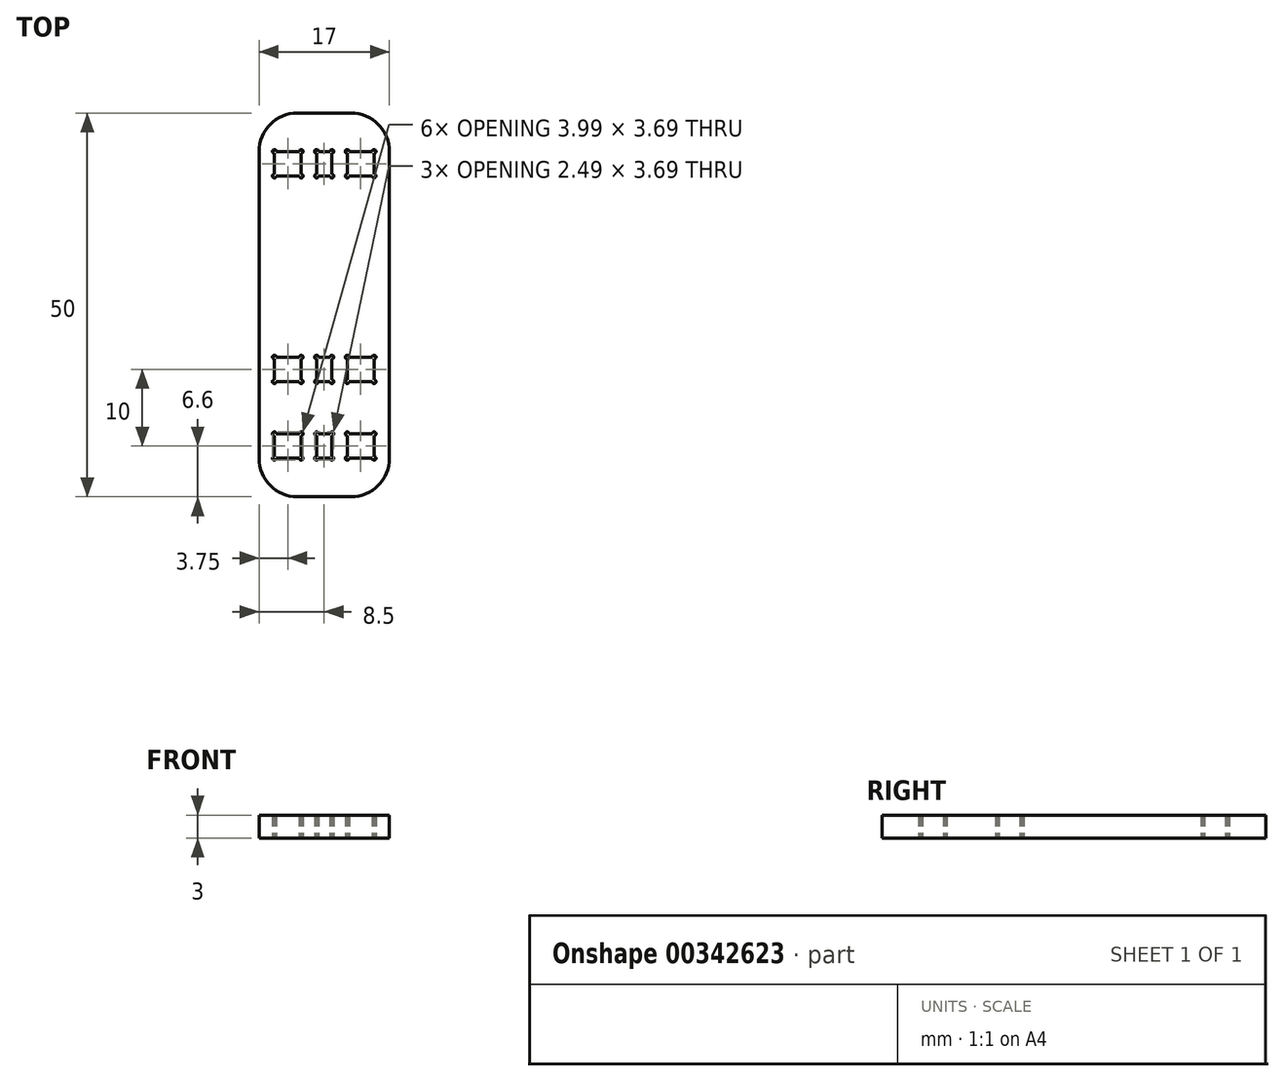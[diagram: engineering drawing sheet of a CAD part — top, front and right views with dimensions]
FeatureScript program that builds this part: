
annotation { "Feature Type Name" : "Feature", "Feature Type Description" : "" }
export const myFeature = defineFeature(function(context is Context, id is Id, definition is map)
    precondition{}
    {
        {
            var Q0;
            Q0=qCreatedBy(makeId("Top.planeOp"),FACE);
            var sketch = newSketch(context, id + "F0", { "sketchPlane" : qUnion([Q0])});
            skLineSegment(sketch, "E0.bottom", {"start": v(-3.5, 50) * mm, "end": v(3.5, 50) * mm});
            skLineSegment(sketch, "E0.top", {"start": v(-3.5, 0) * mm, "end": v(3.5, 0) * mm});
            skLineSegment(sketch, "E0.left", {"start": v(-8.5, 45) * mm, "end": v(-8.5, 5) * mm});
            skLineSegment(sketch, "E0.right", {"start": v(8.5, 45) * mm, "end": v(8.5, 5) * mm});
            skLineSegment(sketch, "E1.bottom", {"start": v(-6.5, 8.2) * mm, "end": v(-3, 8.2) * mm});
            skLineSegment(sketch, "E1.top", {"start": v(-6.5, 5) * mm, "end": v(-3, 5) * mm});
            skLineSegment(sketch, "E1.left", {"start": v(-6.5, 8.2) * mm, "end": v(-6.5, 5) * mm});
            skLineSegment(sketch, "E1.right", {"start": v(-3, 8.2) * mm, "end": v(-3, 5) * mm});
            skLineSegment(sketch, "E2.bottom", {"start": v(-1, 8.2) * mm, "end": v(1, 8.2) * mm});
            skLineSegment(sketch, "E2.top", {"start": v(-1, 5) * mm, "end": v(1, 5) * mm});
            skLineSegment(sketch, "E2.left", {"start": v(-1, 8.2) * mm, "end": v(-1, 5) * mm});
            skLineSegment(sketch, "E2.right", {"start": v(1, 8.2) * mm, "end": v(1, 5) * mm});
            skLineSegment(sketch, "E3.bottom", {"start": v(3, 8.2) * mm, "end": v(6.5, 8.2) * mm});
            skLineSegment(sketch, "E3.top", {"start": v(3, 5) * mm, "end": v(6.5, 5) * mm});
            skLineSegment(sketch, "E3.left", {"start": v(3, 8.2) * mm, "end": v(3, 5) * mm});
            skLineSegment(sketch, "E3.right", {"start": v(6.5, 8.2) * mm, "end": v(6.5, 5) * mm});
            skPoint(sketch, "E4", {"position": v(0, 5) * mm});
            skPoint(sketch, "E5", {"position": v(0, 0) * mm});
            skLineSegment(sketch, "E6", {"start": v(0, 5) * mm, "end": v(0, 0) * mm, "construction": true});
            skCircle(sketch, "E7", {"center": v(-6.5, 8.2) * mm, "radius": 0.25 * mm});
            skCircle(sketch, "E8", {"center": v(-3, 8.2) * mm, "radius": 0.25 * mm});
            skCircle(sketch, "E9", {"center": v(-3, 5) * mm, "radius": 0.25 * mm});
            skCircle(sketch, "E10", {"center": v(-6.5, 5) * mm, "radius": 0.25 * mm});
            skCircle(sketch, "E11", {"center": v(-1, 5) * mm, "radius": 0.25 * mm});
            skCircle(sketch, "E12", {"center": v(-1, 8.2) * mm, "radius": 0.25 * mm});
            skCircle(sketch, "E13.MirrorC", {"center": v(6.5, 5) * mm, "radius": 0.25 * mm});
            skCircle(sketch, "E14.MirrorC", {"center": v(6.5, 8.2) * mm, "radius": 0.25 * mm});
            skCircle(sketch, "E15.MirrorC", {"center": v(3, 8.2) * mm, "radius": 0.25 * mm});
            skCircle(sketch, "E16.MirrorC", {"center": v(3, 5) * mm, "radius": 0.25 * mm});
            skCircle(sketch, "E17.MirrorC", {"center": v(1, 5) * mm, "radius": 0.25 * mm});
            skCircle(sketch, "E18.MirrorC", {"center": v(1, 8.2) * mm, "radius": 0.25 * mm});
            skLineSegment(sketch, "E19", {"start": v(-8.5, 25) * mm, "end": v(8.5, 25) * mm, "construction": true});
            skLineSegment(sketch, "E20.MirrorCS", {"start": v(1, 5) * mm, "end": v(-1, 5) * mm});
            skLineSegment(sketch, "E21.MirrorCS", {"start": v(1, 8.2) * mm, "end": v(-1, 8.2) * mm});
            skLineSegment(sketch, "E22.MirrorCS", {"start": v(6.5, 5) * mm, "end": v(3, 5) * mm});
            skLineSegment(sketch, "E23.MirrorCS", {"start": v(6.5, 8.2) * mm, "end": v(3, 8.2) * mm});
            skLineSegment(sketch, "E24.MirrorCS", {"start": v(-3, 8.2) * mm, "end": v(-6.5, 8.2) * mm});
            skLineSegment(sketch, "E25.MirrorCS", {"start": v(-3, 5) * mm, "end": v(-6.5, 5) * mm});
            skLineSegment(sketch, "E26.MirrorCS", {"start": v(8.5, 25) * mm, "end": v(-8.5, 25) * mm, "construction": true});
            skCircle(sketch, "E27.MirrorC", {"center": v(-3, 45) * mm, "radius": 0.25 * mm});
            skCircle(sketch, "E28.MirrorC", {"center": v(-1, 45) * mm, "radius": 0.25 * mm});
            skCircle(sketch, "E29.MirrorC", {"center": v(-6.5, 41.8) * mm, "radius": 0.25 * mm});
            skCircle(sketch, "E30.MirrorC", {"center": v(-6.5, 45) * mm, "radius": 0.25 * mm});
            skLineSegment(sketch, "E31.MirrorCS", {"start": v(1, 45) * mm, "end": v(-1, 45) * mm});
            skCircle(sketch, "E32.MirrorC", {"center": v(-1, 41.8) * mm, "radius": 0.25 * mm});
            skCircle(sketch, "E33.MirrorC", {"center": v(6.5, 45) * mm, "radius": 0.25 * mm});
            skCircle(sketch, "E34.MirrorC", {"center": v(3, 41.8) * mm, "radius": 0.25 * mm});
            skCircle(sketch, "E35.MirrorC", {"center": v(3, 45) * mm, "radius": 0.25 * mm});
            skCircle(sketch, "E36.MirrorC", {"center": v(6.5, 41.8) * mm, "radius": 0.25 * mm});
            skLineSegment(sketch, "E37.MirrorCS", {"start": v(1, 41.8) * mm, "end": v(-1, 41.8) * mm});
            skCircle(sketch, "E38.MirrorC", {"center": v(1, 45) * mm, "radius": 0.25 * mm});
            skCircle(sketch, "E39.MirrorC", {"center": v(-3, 41.8) * mm, "radius": 0.25 * mm});
            skCircle(sketch, "E40.MirrorC", {"center": v(1, 41.8) * mm, "radius": 0.25 * mm});
            skLineSegment(sketch, "E41.MirrorCS", {"start": v(-1, 45) * mm, "end": v(1, 45) * mm});
            skLineSegment(sketch, "E42.MirrorCS", {"start": v(-1, 41.8) * mm, "end": v(1, 41.8) * mm});
            skLineSegment(sketch, "E43.MirrorCS", {"start": v(-3, 45) * mm, "end": v(-6.5, 45) * mm});
            skLineSegment(sketch, "E44.MirrorCS", {"start": v(-3, 41.8) * mm, "end": v(-6.5, 41.8) * mm});
            skLineSegment(sketch, "E45.MirrorCS", {"start": v(6.5, 41.8) * mm, "end": v(6.5, 45) * mm});
            skLineSegment(sketch, "E46.MirrorCS", {"start": v(-6.5, 41.8) * mm, "end": v(-6.5, 45) * mm});
            skLineSegment(sketch, "E47.MirrorCS", {"start": v(6.5, 41.8) * mm, "end": v(3, 41.8) * mm});
            skLineSegment(sketch, "E48.MirrorCS", {"start": v(-3, 41.8) * mm, "end": v(-3, 45) * mm});
            skLineSegment(sketch, "E49.MirrorCS", {"start": v(1, 41.8) * mm, "end": v(1, 45) * mm});
            skLineSegment(sketch, "E50.MirrorCS", {"start": v(6.5, 45) * mm, "end": v(3, 45) * mm});
            skLineSegment(sketch, "E51.MirrorCS", {"start": v(3, 41.8) * mm, "end": v(3, 45) * mm});
            skPoint(sketch, "E52.MirrorP", {"position": v(0, 45) * mm});
            skLineSegment(sketch, "E53.MirrorCS", {"start": v(-1, 41.8) * mm, "end": v(-1, 45) * mm});
            skLineSegment(sketch, "E54.MirrorCS", {"start": v(-6.5, 45) * mm, "end": v(-3, 45) * mm});
            skLineSegment(sketch, "E55.MirrorCS", {"start": v(3, 41.8) * mm, "end": v(6.5, 41.8) * mm});
            skLineSegment(sketch, "E56.MirrorCS", {"start": v(-6.5, 41.8) * mm, "end": v(-3, 41.8) * mm});
            skLineSegment(sketch, "E57.MirrorCS", {"start": v(3, 45) * mm, "end": v(6.5, 45) * mm});
            skLineSegment(sketch, "E58.0.1.0", {"start": v(3, 18.2) * mm, "end": v(6.5, 18.2) * mm});
            skLineSegment(sketch, "E58.0.1.1", {"start": v(6.5, 18.2) * mm, "end": v(6.5, 15) * mm});
            skLineSegment(sketch, "E58.0.1.2", {"start": v(3, 15) * mm, "end": v(6.5, 15) * mm});
            skLineSegment(sketch, "E58.0.1.3", {"start": v(-3, 18.2) * mm, "end": v(-3, 15) * mm});
            skLineSegment(sketch, "E58.0.1.4", {"start": v(1, 18.2) * mm, "end": v(1, 15) * mm});
            skLineSegment(sketch, "E58.0.1.5", {"start": v(-1, 18.2) * mm, "end": v(-1, 15) * mm});
            skPoint(sketch, "E58.0.1.6", {"position": v(0, 15) * mm});
            skLineSegment(sketch, "E58.0.1.7", {"start": v(3, 18.2) * mm, "end": v(3, 15) * mm});
            skLineSegment(sketch, "E58.0.1.8", {"start": v(1, 18.2) * mm, "end": v(1, 15) * mm});
            skLineSegment(sketch, "E58.0.1.9", {"start": v(3, 18.2) * mm, "end": v(3, 15) * mm});
            skLineSegment(sketch, "E58.0.1.10", {"start": v(-1, 18.2) * mm, "end": v(-1, 15) * mm});
            skPoint(sketch, "E58.0.1.11", {"position": v(0, 15) * mm});
            skLineSegment(sketch, "E58.0.1.12", {"start": v(-6.5, 15) * mm, "end": v(-3, 15) * mm});
            skLineSegment(sketch, "E58.0.1.13", {"start": v(-6.5, 18.2) * mm, "end": v(-6.5, 15) * mm});
            skLineSegment(sketch, "E58.0.1.14", {"start": v(-3, 18.2) * mm, "end": v(-3, 15) * mm});
            skLineSegment(sketch, "E58.0.1.15", {"start": v(6.5, 18.2) * mm, "end": v(3, 18.2) * mm});
            skLineSegment(sketch, "E58.0.1.16", {"start": v(3, 15) * mm, "end": v(6.5, 15) * mm});
            skLineSegment(sketch, "E58.0.1.17", {"start": v(6.5, 18.2) * mm, "end": v(6.5, 15) * mm});
            skLineSegment(sketch, "E58.0.1.18", {"start": v(-6.5, 18.2) * mm, "end": v(-3, 18.2) * mm});
            skLineSegment(sketch, "E58.0.1.19", {"start": v(-6.5, 15) * mm, "end": v(-3, 15) * mm});
            skLineSegment(sketch, "E58.0.1.20", {"start": v(-6.5, 18.2) * mm, "end": v(-6.5, 15) * mm});
            skLineSegment(sketch, "E58.0.1.21", {"start": v(-1, 18.2) * mm, "end": v(-1, 15) * mm});
            skLineSegment(sketch, "E58.0.1.22", {"start": v(1, 18.2) * mm, "end": v(1, 15) * mm});
            skLineSegment(sketch, "E58.0.1.23", {"start": v(-3, 18.2) * mm, "end": v(-3, 15) * mm});
            skLineSegment(sketch, "E58.0.1.24", {"start": v(-6.5, 18.2) * mm, "end": v(-3, 18.2) * mm});
            skLineSegment(sketch, "E58.0.1.25", {"start": v(6.5, 18.2) * mm, "end": v(6.5, 15) * mm});
            skLineSegment(sketch, "E58.0.1.26", {"start": v(3, 18.2) * mm, "end": v(3, 15) * mm});
            skPoint(sketch, "E58.0.1.27", {"position": v(0, 15) * mm});
            skLineSegment(sketch, "E58.0.1.28", {"start": v(6.5, 15) * mm, "end": v(3, 15) * mm});
            skLineSegment(sketch, "E58.0.1.29", {"start": v(3, 18.2) * mm, "end": v(6.5, 18.2) * mm});
            skLineSegment(sketch, "E58.0.1.30", {"start": v(-3, 18.2) * mm, "end": v(-6.5, 18.2) * mm});
            skLineSegment(sketch, "E58.0.1.31", {"start": v(3, 18.2) * mm, "end": v(3, 15) * mm});
            skPoint(sketch, "E58.0.1.32", {"position": v(0, 15) * mm});
            skLineSegment(sketch, "E58.0.1.33", {"start": v(-3, 15) * mm, "end": v(-6.5, 15) * mm});
            skLineSegment(sketch, "E58.0.1.34", {"start": v(6.5, 15) * mm, "end": v(3, 15) * mm});
            skLineSegment(sketch, "E58.0.1.35", {"start": v(1, 18.2) * mm, "end": v(1, 15) * mm});
            skLineSegment(sketch, "E58.0.1.36", {"start": v(-3, 18.2) * mm, "end": v(-3, 15) * mm});
            skLineSegment(sketch, "E58.0.1.37", {"start": v(6.5, 18.2) * mm, "end": v(3, 18.2) * mm});
            skLineSegment(sketch, "E58.0.1.38", {"start": v(-1, 18.2) * mm, "end": v(-1, 15) * mm});
            skLineSegment(sketch, "E58.0.1.39", {"start": v(6.5, 18.2) * mm, "end": v(6.5, 15) * mm});
            skLineSegment(sketch, "E58.0.1.40", {"start": v(-6.5, 18.2) * mm, "end": v(-6.5, 15) * mm});
            skLineSegment(sketch, "E58.0.1.41", {"start": v(-3, 15) * mm, "end": v(-6.5, 15) * mm});
            skLineSegment(sketch, "E58.0.1.42", {"start": v(-3, 18.2) * mm, "end": v(-6.5, 18.2) * mm});
            skLineSegment(sketch, "E58.0.1.43", {"start": v(-6.5, 18.2) * mm, "end": v(-6.5, 15) * mm});
            skCircle(sketch, "E58.0.1.44", {"center": v(1, 18.2) * mm, "radius": 0.25 * mm});
            skCircle(sketch, "E58.0.1.45", {"center": v(6.5, 15) * mm, "radius": 0.25 * mm});
            skLineSegment(sketch, "E58.0.1.46", {"start": v(-1, 18.2) * mm, "end": v(1, 18.2) * mm});
            skCircle(sketch, "E58.0.1.47", {"center": v(-6.5, 18.2) * mm, "radius": 0.25 * mm});
            skLineSegment(sketch, "E58.0.1.48", {"start": v(-1, 15) * mm, "end": v(1, 15) * mm});
            skCircle(sketch, "E58.0.1.49", {"center": v(-6.5, 15) * mm, "radius": 0.25 * mm});
            skCircle(sketch, "E58.0.1.50", {"center": v(6.5, 18.2) * mm, "radius": 0.25 * mm});
            skCircle(sketch, "E58.0.1.51", {"center": v(-1, 15) * mm, "radius": 0.25 * mm});
            skCircle(sketch, "E58.0.1.52", {"center": v(3, 18.2) * mm, "radius": 0.25 * mm});
            skCircle(sketch, "E58.0.1.53", {"center": v(-1, 18.2) * mm, "radius": 0.25 * mm});
            skCircle(sketch, "E58.0.1.54", {"center": v(-3, 15) * mm, "radius": 0.25 * mm});
            skCircle(sketch, "E58.0.1.55", {"center": v(-3, 18.2) * mm, "radius": 0.25 * mm});
            skCircle(sketch, "E58.0.1.56", {"center": v(3, 15) * mm, "radius": 0.25 * mm});
            skCircle(sketch, "E58.0.1.57", {"center": v(1, 15) * mm, "radius": 0.25 * mm});
            skCircle(sketch, "E58.0.1.58", {"center": v(1, 18.2) * mm, "radius": 0.25 * mm});
            skCircle(sketch, "E58.0.1.59", {"center": v(-6.5, 15) * mm, "radius": 0.25 * mm});
            skCircle(sketch, "E58.0.1.60", {"center": v(6.5, 15) * mm, "radius": 0.25 * mm});
            skLineSegment(sketch, "E58.0.1.61", {"start": v(-1, 15) * mm, "end": v(1, 15) * mm});
            skCircle(sketch, "E58.0.1.62", {"center": v(-1, 15) * mm, "radius": 0.25 * mm});
            skCircle(sketch, "E58.0.1.63", {"center": v(-3, 18.2) * mm, "radius": 0.25 * mm});
            skCircle(sketch, "E58.0.1.64", {"center": v(-3, 15) * mm, "radius": 0.25 * mm});
            skCircle(sketch, "E58.0.1.65", {"center": v(-1, 18.2) * mm, "radius": 0.25 * mm});
            skCircle(sketch, "E58.0.1.66", {"center": v(3, 18.2) * mm, "radius": 0.25 * mm});
            skCircle(sketch, "E58.0.1.67", {"center": v(6.5, 18.2) * mm, "radius": 0.25 * mm});
            skLineSegment(sketch, "E58.0.1.68", {"start": v(-1, 18.2) * mm, "end": v(1, 18.2) * mm});
            skCircle(sketch, "E58.0.1.69", {"center": v(3, 15) * mm, "radius": 0.25 * mm});
            skCircle(sketch, "E58.0.1.70", {"center": v(-6.5, 18.2) * mm, "radius": 0.25 * mm});
            skCircle(sketch, "E58.0.1.71", {"center": v(1, 15) * mm, "radius": 0.25 * mm});
            skCircle(sketch, "E58.0.1.72", {"center": v(-3, 15) * mm, "radius": 0.25 * mm});
            skCircle(sketch, "E58.0.1.73", {"center": v(-6.5, 15) * mm, "radius": 0.25 * mm});
            skCircle(sketch, "E58.0.1.74", {"center": v(-1, 18.2) * mm, "radius": 0.25 * mm});
            skLineSegment(sketch, "E58.0.1.75", {"start": v(1, 15) * mm, "end": v(-1, 15) * mm});
            skCircle(sketch, "E58.0.1.76", {"center": v(1, 15) * mm, "radius": 0.25 * mm});
            skCircle(sketch, "E58.0.1.77", {"center": v(-1, 15) * mm, "radius": 0.25 * mm});
            skCircle(sketch, "E58.0.1.78", {"center": v(6.5, 15) * mm, "radius": 0.25 * mm});
            skCircle(sketch, "E58.0.1.79", {"center": v(6.5, 18.2) * mm, "radius": 0.25 * mm});
            skCircle(sketch, "E58.0.1.80", {"center": v(3, 18.2) * mm, "radius": 0.25 * mm});
            skLineSegment(sketch, "E58.0.1.81", {"start": v(1, 18.2) * mm, "end": v(-1, 18.2) * mm});
            skCircle(sketch, "E58.0.1.82", {"center": v(3, 15) * mm, "radius": 0.25 * mm});
            skCircle(sketch, "E58.0.1.83", {"center": v(1, 18.2) * mm, "radius": 0.25 * mm});
            skCircle(sketch, "E58.0.1.84", {"center": v(-6.5, 18.2) * mm, "radius": 0.25 * mm});
            skCircle(sketch, "E58.0.1.85", {"center": v(-3, 18.2) * mm, "radius": 0.25 * mm});
            skCircle(sketch, "E58.0.1.86", {"center": v(6.5, 18.2) * mm, "radius": 0.25 * mm});
            skCircle(sketch, "E58.0.1.87", {"center": v(3, 15) * mm, "radius": 0.25 * mm});
            skCircle(sketch, "E58.0.1.88", {"center": v(6.5, 15) * mm, "radius": 0.25 * mm});
            skCircle(sketch, "E58.0.1.89", {"center": v(3, 18.2) * mm, "radius": 0.25 * mm});
            skCircle(sketch, "E58.0.1.90", {"center": v(-1, 18.2) * mm, "radius": 0.25 * mm});
            skLineSegment(sketch, "E58.0.1.91", {"start": v(1, 15) * mm, "end": v(-1, 15) * mm});
            skCircle(sketch, "E58.0.1.92", {"center": v(-6.5, 15) * mm, "radius": 0.25 * mm});
            skLineSegment(sketch, "E58.0.1.93", {"start": v(1, 18.2) * mm, "end": v(-1, 18.2) * mm});
            skCircle(sketch, "E58.0.1.94", {"center": v(1, 18.2) * mm, "radius": 0.25 * mm});
            skCircle(sketch, "E58.0.1.95", {"center": v(-3, 15) * mm, "radius": 0.25 * mm});
            skCircle(sketch, "E58.0.1.96", {"center": v(-1, 15) * mm, "radius": 0.25 * mm});
            skCircle(sketch, "E58.0.1.97", {"center": v(-6.5, 18.2) * mm, "radius": 0.25 * mm});
            skCircle(sketch, "E58.0.1.98", {"center": v(-3, 18.2) * mm, "radius": 0.25 * mm});
            skCircle(sketch, "E58.0.1.99", {"center": v(1, 15) * mm, "radius": 0.25 * mm});
            skLineSegment(sketch, "E58.direction1", {"start": v(-6.5, 5) * mm, "end": v(18.5, 5) * mm, "construction": true});
            skLineSegment(sketch, "E58.direction2", {"start": v(-6.5, 5) * mm, "end": v(-6.5, 15) * mm, "construction": true});
            skPoint(sketch, "E59.visualSharp", {"position": v(-8.5, 50) * mm});
            skArc(sketch, "E59.filletArc", {"start": v(-3.5, 50) * mm, "mid": v(-7.04, 48.54) * mm, "end": v(-8.5, 45) * mm});
            skPoint(sketch, "E60.visualSharp", {"position": v(8.5, 50) * mm});
            skArc(sketch, "E60.filletArc", {"start": v(8.5, 45) * mm, "mid": v(7.04, 48.54) * mm, "end": v(3.5, 50) * mm});
            skPoint(sketch, "E61.visualSharp", {"position": v(8.5, 0) * mm});
            skArc(sketch, "E61.filletArc", {"start": v(3.5, 0) * mm, "mid": v(7.04, 1.46) * mm, "end": v(8.5, 5) * mm});
            skPoint(sketch, "E62.visualSharp", {"position": v(-8.5, 0) * mm});
            skArc(sketch, "E62.filletArc", {"start": v(-8.5, 5) * mm, "mid": v(-7.04, 1.46) * mm, "end": v(-3.5, 0) * mm});
            skSolve(sketch);
        }
        {
            var Q0;
            Q0=makeQuery(id+"F0.imprint","IMPRINT",FACE,{"disambiguationData":[TD([[makeQuery(id+"F0.imprint","IMPRINT",EDGE,{"derivedFrom":sQuery(id+"F0.wireOp",EDGE,"E0.bottom")}),-1.0]])]});
            extrude(context, id + "F1", {"entities" : qUnion([Q0]), "depth" : 3 * mm});
        }
    });
